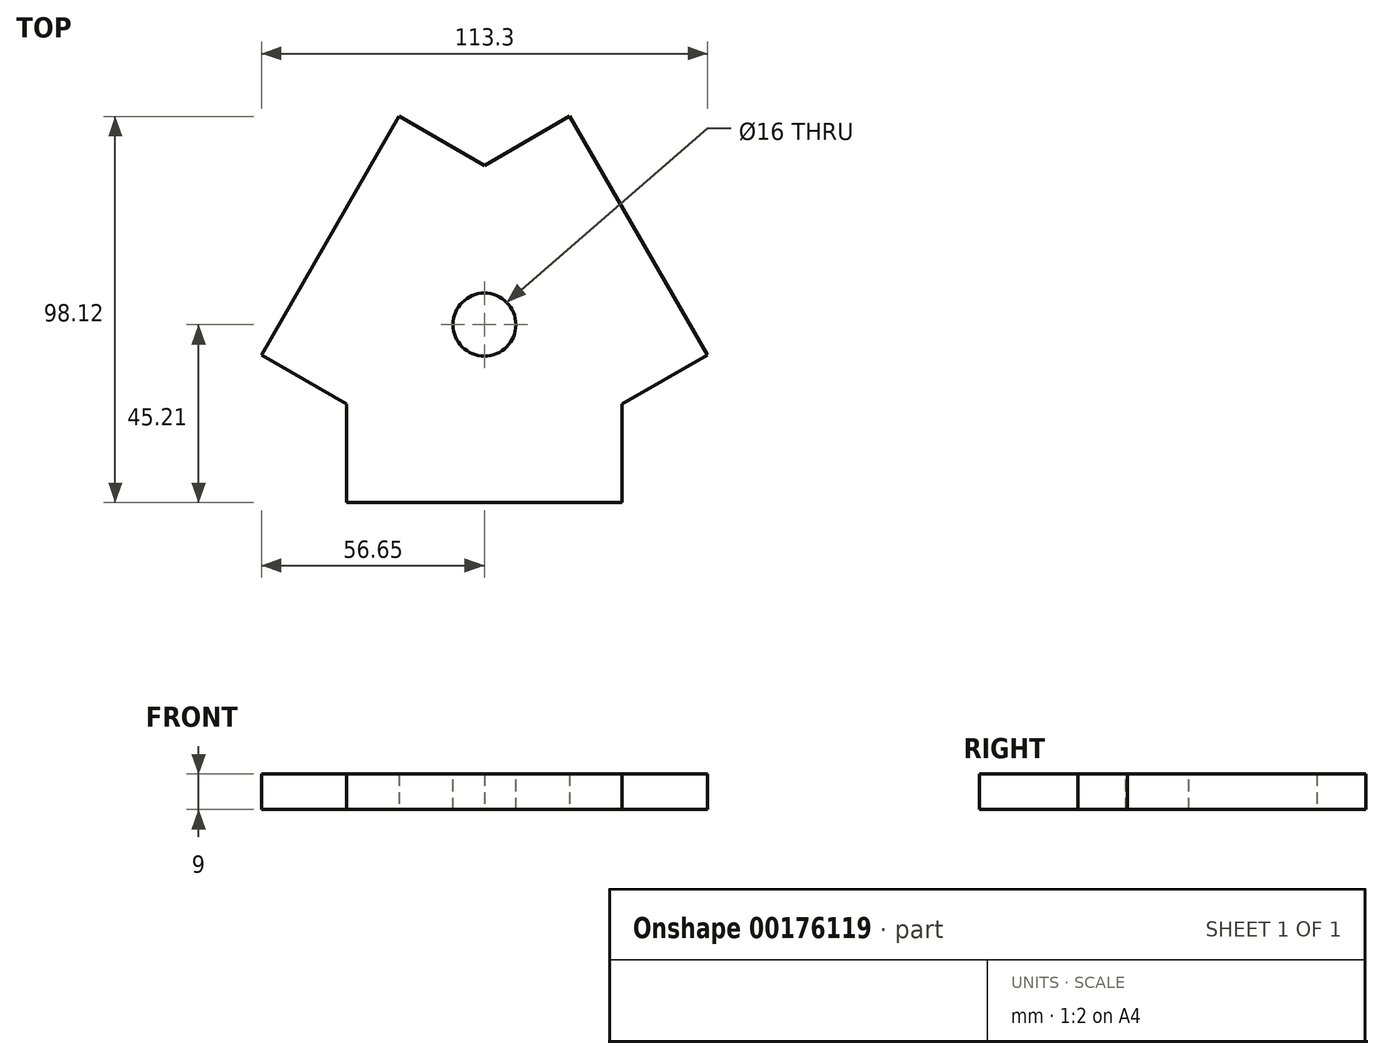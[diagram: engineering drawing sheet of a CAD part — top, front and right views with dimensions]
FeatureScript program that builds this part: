
annotation { "Feature Type Name" : "Feature", "Feature Type Description" : "" }
export const myFeature = defineFeature(function(context is Context, id is Id, definition is map)
    precondition{}
    {
        {
            var Q0;
            Q0=qCreatedBy(makeId("Top.planeOp"),FACE);
            var sketch = newSketch(context, id + "F0", { "sketchPlane" : qUnion([Q0])});
            skCircle(sketch, "E0.cCircle", {"center": v(0, 0) * mm, "radius": 20.2 * mm, "construction": true});
            skLineSegment(sketch, "E0.0", {"start": v(35, -20.2) * mm, "end": v(-35, -20.2) * mm});
            skLineSegment(sketch, "E0.1", {"start": v(-35, -20.2) * mm, "end": v(0, 40.41) * mm});
            skLineSegment(sketch, "E0.2", {"start": v(0, 40.41) * mm, "end": v(35, -20.2) * mm});
            skPoint(sketch, "E0.0.midPoint", {"position": v(0, -20.2) * mm});
            skSolve(sketch);
        }
        {
            var Q0;
            Q0 = qSketchRegion(id + "F0", true);
            extrude(context, id + "F1", {"entities" : qUnion([Q0]), "depth" : 9 * mm});
        }
        {
            var Q0;
            Q0=makeQuery(id+"F1.opExtrude","SWEPT_FACE",FACE,{"disambiguationData":[OSD([sQuery(id+"F0.wireOp",EDGE,"E0.0")])]});
            extrude(context, id + "F2", {"entities" : qUnion([Q0]), "operationType" : NewBodyOperationType.ADD, "depth" : 25 * mm});
        }
        {
            var Q0;
            Q0=makeQuery(id+"F1.opExtrude","SWEPT_FACE",FACE,{"disambiguationData":[OSD([sQuery(id+"F0.wireOp",EDGE,"E0.2")])]});
            extrude(context, id + "F3", {"entities" : qUnion([Q0]), "operationType" : NewBodyOperationType.ADD, "depth" : 25 * mm});
        }
        {
            var Q0;
            Q0=makeQuery(id+"F1.opExtrude","SWEPT_FACE",FACE,{"disambiguationData":[OSD([sQuery(id+"F0.wireOp",EDGE,"E0.1")])]});
            extrude(context, id + "F4", {"entities" : qUnion([Q0]), "operationType" : NewBodyOperationType.ADD, "depth" : 25 * mm});
        }
        {
            var Q0;
            {var subQ0=sQuery(id+"F0.wireOp",EDGE,"E0.1");var subQ1=sQuery(id+"F0.wireOp",EDGE,"E0.2");var subQ2=sQuery(id+"F0.wireOp",EDGE,"E0.0");Q0=makeQuery(id+"F4.boolean.opBoolean","MERGE",FACE,{"derivedFrom":[makeQuery(id+"F3.boolean.opBoolean","MERGE",FACE,{"derivedFrom":[makeQuery(id+"F2.boolean.opBoolean","MERGE",FACE,{"derivedFrom":[makeQuery(id+"F1.opExtrude","CAP_FACE",FACE,{"disambiguationData":[OSD([subQ2,subQ0,subQ1])],"isStart":false}),makeQuery(id+"F2.opExtrude","SWEPT_FACE",FACE,{"disambiguationData":[OSD([subQ2]),TDD([makeQuery(id+"F1.opExtrude","CAP_EDGE",EDGE,{"disambiguationData":[OSD([subQ2])],"isStart":false})])]})]}),makeQuery(id+"F3.opExtrude","SWEPT_FACE",FACE,{"disambiguationData":[OSD([subQ1]),TDD([makeQuery(id+"F1.opExtrude","CAP_EDGE",EDGE,{"disambiguationData":[OSD([subQ1])],"isStart":false})])]})]}),makeQuery(id+"F4.opExtrude","SWEPT_FACE",FACE,{"disambiguationData":[OSD([subQ0]),TDD([makeQuery(id+"F1.opExtrude","CAP_EDGE",EDGE,{"disambiguationData":[OSD([subQ0])],"isStart":false})])]})]});}
            var sketch = newSketch(context, id + "F5", { "sketchPlane" : qUnion([Q0])});
            skCircle(sketch, "E1", {"center": v(0, 0) * mm, "radius": 8 * mm});
            skSolve(sketch);
        }
        {
            var Q0;
            Q0=makeQuery(id+"F5.imprint","IMPRINT",FACE,{"disambiguationData":[TD([[makeQuery(id+"F5.imprint","IMPRINT",EDGE,{"derivedFrom":sQuery(id+"F5.wireOp",EDGE,"E1")}),1.0]])]});
            extrude(context, id + "F6", {"entities" : qUnion([Q0]), "operationType" : NewBodyOperationType.REMOVE, "oppositeDirection" : true, "depth" : 25 * mm});
        }
    });
